# Revit family: Fioriera MARTE
name_source: partatom
category: Modelli generici
revit_build: Autodesk Revit 2018 (Build: 20170223_1515(x64)
units: mm (PartAtom-declared; Revit-internal decimal feet)

## family parameters
Basato su piano di lavoro = No
Condiviso = No
Punto di calcolo locali = No
Può ospitare armatura = No
Quota connettore circolare = Usa diametro
Sempre verticale = Sì
Taglio con vuoti quando caricato = No
Tipo di parte = Normale

## types (4) — shared parameters
BIM Name = MARTE - 1225 Lt
BIM Object Type = FIORIERE - PLANTERS
Code = 0FIPP004
Descrizione Tecnica Famiglia = "Fioriera mod. “MARTE” costituita da una fioriera monolitica dotata di scarichi di fondo."
Designer = BELLITALIA DESIGN
Dimensions = ⌀=1900 mm h=1100 mm
Family Name = PIANETI
Fissaggio = Appoggio
Fixings = Freestanding
IFC = Furniture and Furnishings
MASTERFORMAT 2014 (DESCRIPTION/CODE) = Planters / 32 94 33
OMNICLASS (DESCRIPTION/CODE) = Planters / 23-11 27 13 17
Technical Description Family = Planter model "MARTE" consists of a monolithic planter equipped with bottom drains.
UNICLASS 1.4 (DESCRIPTION/CODE) = Planters / L8721
UNICLASS 2.0 (DESCRIPTION/CODE) = Herb Planters / Pr 45 63 63 337
UNIFORMAT II (DESCRIPTION/CODE) = Furnishings / E20
UNSPSC CATEGORY (CODE) = 56
URL Eng = https://www.bellitalia.net
URL Ita = https://www.bellitalia.net
Weight ( kg) = 1225 Kg

## per-type parameters (varying)
| type | Descrizione Tecnica per Codice | MATERIALE FIORIERA | Materiale Principale | Materiale Secondario | Primary Material | Secondary Material | Technical Description for Article |
| 0FIPP004 - GRANITO - 1225 Lt | FIORIERA MARTE IN GRANITO (COLORE A SCELTA) BOCCIARDATA VERNICE ANTIDECADIMENTO | GRANITO | Granito Bianco | Pietre di Granito | White Granite | Reconstituted Granite | MARTE PLANTER IN GRANITO (COLOR TO BE CHOSEN) BUSH-HAMMERED  ANTI-DECAY VARNISH |
| 0FIPP004 - VERDE ALPI - 1225 Lt | FIORIERA MARS IN VERNICE VERDE ALPI BOCCIARDATA ANTIDECADENTE VERNICE ANTIDECADIMENTO | VERDE ALPI | Pietre Preziose Ricostituite Verde Alpi | Pietre Preziose Ricostituite | Green Alps Reconstituted Precious Stones | Reconstituted Precious Stone | MARTE PLANTER IN GREEN ALPS BUSH-HAMMERED ANTI-DECAY VARNISH |
| 0FIPP004 - MURANO - 1225 Lt | FIORIERA MARTE IN MURANO (COLORE A SCELTA) BOCCIARDATA VERNICE ANTIDECADIMENTO | MURANO | Murano Bianco | Murano | White Murano | Murano | MARTE PLANTER IN MURANO (COLOR TO BE CHOSEN) BUSH-HAMMERED  ANTI-DECAY VARNISH |
| 0FIPP004 - PIETRE PREZIOSE - 1225 Lt | MARTE FIORIERA IN PIETRE PREZIOSE (COLORE DA SCELTA TRANNE VERDE ALPI) VERNICE ANTIDECADIMENTO BOCCIARDATA | PIETRE PREZIOSE | Pietre Preziose Ricostituite Bianco Carrara | Pietre Preziose Ricostituite | White Carrara Reconstituted Gemstones | Reconstituted Precious Stone | MARTE PLANTER IN PRECIOUS STONES (COLOR TO BE CHOSEN EXCEPT  GREEN ALPS) BUSH-HAMMERED ANTI-DECAY VARNISH |
